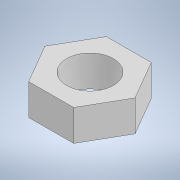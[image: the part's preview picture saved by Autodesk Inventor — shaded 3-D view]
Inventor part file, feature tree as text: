
AUTODESK INVENTOR PART (.ipt)
format: ipt  version: 2022 (Build 260153000, 153)  size: 102,912 bytes
history: native  units: in
note: dims shown in document units (in); Inventor stores cm internally (conversion verified against a paired STEP export)
features: extrude x2, sketch x2
ambient origin geometry x8: Origin, YZ Plane, XZ Plane, XY Plane, X Axis, Y Axis, Z Axis, Center Point
bodies: Solid1 (feature_tree)
feature tree (4):
  extrude  "Extrusion1"  Depth=0.0787in TaperAngle=0.0deg
  extrude  "Extrusion3"  Depth=0.3937in TaperAngle=0.0deg
  sketch  "Sketch1"  dims[d0=0.1969in d1=0.0787in d2=0.0in]
  sketch  "Sketch3"  dims[d6=0.1181in d7=0.3937in d8=0.0in]
